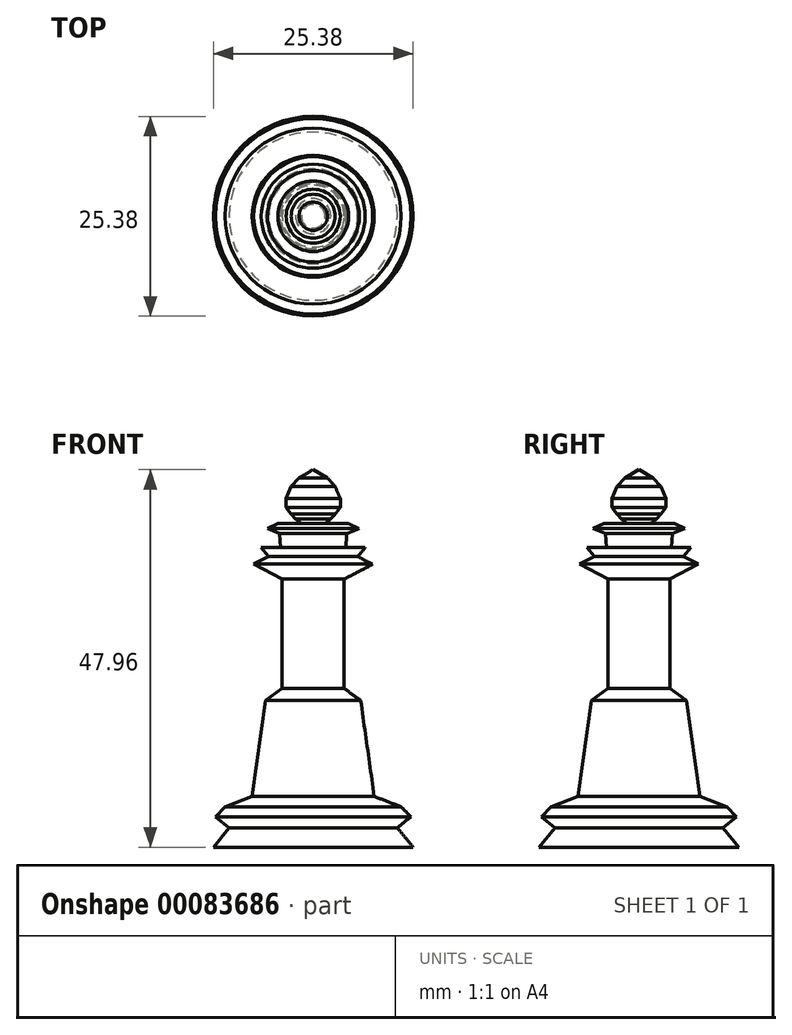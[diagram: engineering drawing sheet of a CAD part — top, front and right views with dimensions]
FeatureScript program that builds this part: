
annotation { "Feature Type Name" : "Feature", "Feature Type Description" : "" }
export const myFeature = defineFeature(function(context is Context, id is Id, definition is map)
    precondition{}
    {
        {
            var Q0;
            Q0=qCreatedBy(makeId("Front.planeOp"),FACE);
            var sketch = newSketch(context, id + "F0", { "sketchPlane" : qUnion([Q0])});
            skLineSegment(sketch, "E0", {"start": v(0, -39.62) * mm, "end": v(10.69, -39.62) * mm});
            skLineSegment(sketch, "E1", {"start": v(10.69, -39.62) * mm, "end": v(12.7, -39.62) * mm});
            skLineSegment(sketch, "E2", {"start": v(12.7, -39.62) * mm, "end": v(10.69, -37.17) * mm});
            skLineSegment(sketch, "E3", {"start": v(10.69, -37.17) * mm, "end": v(12.4, -35.76) * mm});
            skLineSegment(sketch, "E4", {"start": v(12.4, -35.76) * mm, "end": v(11.17, -34.5) * mm});
            skLineSegment(sketch, "E5", {"start": v(11.17, -34.5) * mm, "end": v(7.75, -33.17) * mm});
            skLineSegment(sketch, "E6", {"start": v(7.75, -33.17) * mm, "end": v(6.03, -20.99) * mm});
            skLineSegment(sketch, "E7", {"start": v(6.03, -20.99) * mm, "end": v(3.94, -19.47) * mm});
            skLineSegment(sketch, "E8", {"start": v(3.94, -19.47) * mm, "end": v(3.94, -5.57) * mm});
            skLineSegment(sketch, "E9", {"start": v(3.94, -5.57) * mm, "end": v(7.56, -3.67) * mm});
            skLineSegment(sketch, "E10", {"start": v(7.56, -3.67) * mm, "end": v(5.65, -2.72) * mm});
            skLineSegment(sketch, "E11", {"start": v(5.65, -2.72) * mm, "end": v(6.6, -1.55) * mm});
            skPoint(sketch, "E11.endSnap0", {"position": v(6.6, -3.2) * mm});
            skLineSegment(sketch, "E12", {"start": v(6.6, -1.55) * mm, "end": v(5.65, -1.55) * mm});
            skLineSegment(sketch, "E13", {"start": v(5.65, -1.55) * mm, "end": v(4.13, -1.55) * mm});
            skLineSegment(sketch, "E14", {"start": v(4.13, -1.55) * mm, "end": v(4.27, 0.21) * mm});
            skLineSegment(sketch, "E15", {"start": v(4.27, 0.21) * mm, "end": v(5.82, 0.85) * mm});
            skLineSegment(sketch, "E16", {"start": v(5.82, 0.85) * mm, "end": v(4.48, 1.48) * mm});
            skLineSegment(sketch, "E17", {"start": v(4.48, 1.48) * mm, "end": v(0, 1.48) * mm});
            skLineSegment(sketch, "E18", {"start": v(0, 1.48) * mm, "end": v(0, -39.62) * mm});
            skLineSegment(sketch, "E19", {"start": v(1.5, 1.48) * mm, "end": v(2.24, 2.1) * mm});
            skPoint(sketch, "E19.endSnap0", {"position": v(2.24, 1.48) * mm});
            skLineSegment(sketch, "E20", {"start": v(2.24, 2.1) * mm, "end": v(2.8, 2.68) * mm});
            skLineSegment(sketch, "E21", {"start": v(2.8, 2.68) * mm, "end": v(3.43, 3.56) * mm});
            skLineSegment(sketch, "E22", {"start": v(3.43, 3.56) * mm, "end": v(3.43, 4.67) * mm});
            skLineSegment(sketch, "E23", {"start": v(3.43, 4.67) * mm, "end": v(2.8, 6.18) * mm});
            skLineSegment(sketch, "E24", {"start": v(2.8, 6.18) * mm, "end": v(1.8, 7.3) * mm});
            skLineSegment(sketch, "E25", {"start": v(1.8, 7.3) * mm, "end": v(0, 8.34) * mm});
            skPoint(sketch, "E26.endSnap0", {"position": v(0.9, 7.82) * mm});
            skLineSegment(sketch, "E27", {"start": v(0, 8.34) * mm, "end": v(0, 1.48) * mm});
            skSolve(sketch);
        }
        {
            var Q0;
            Q0 = qSketchRegion(id + "F0", true);
            var Q1;
            Q1=sQuery(id+"F0.wireOp",EDGE,"E27");
            revolve(context, id + "F1", {"entities" : qUnion([Q0]), "axis" : qUnion([Q1]), "revolveType" : RevolveType.FULL});
        }
    });
